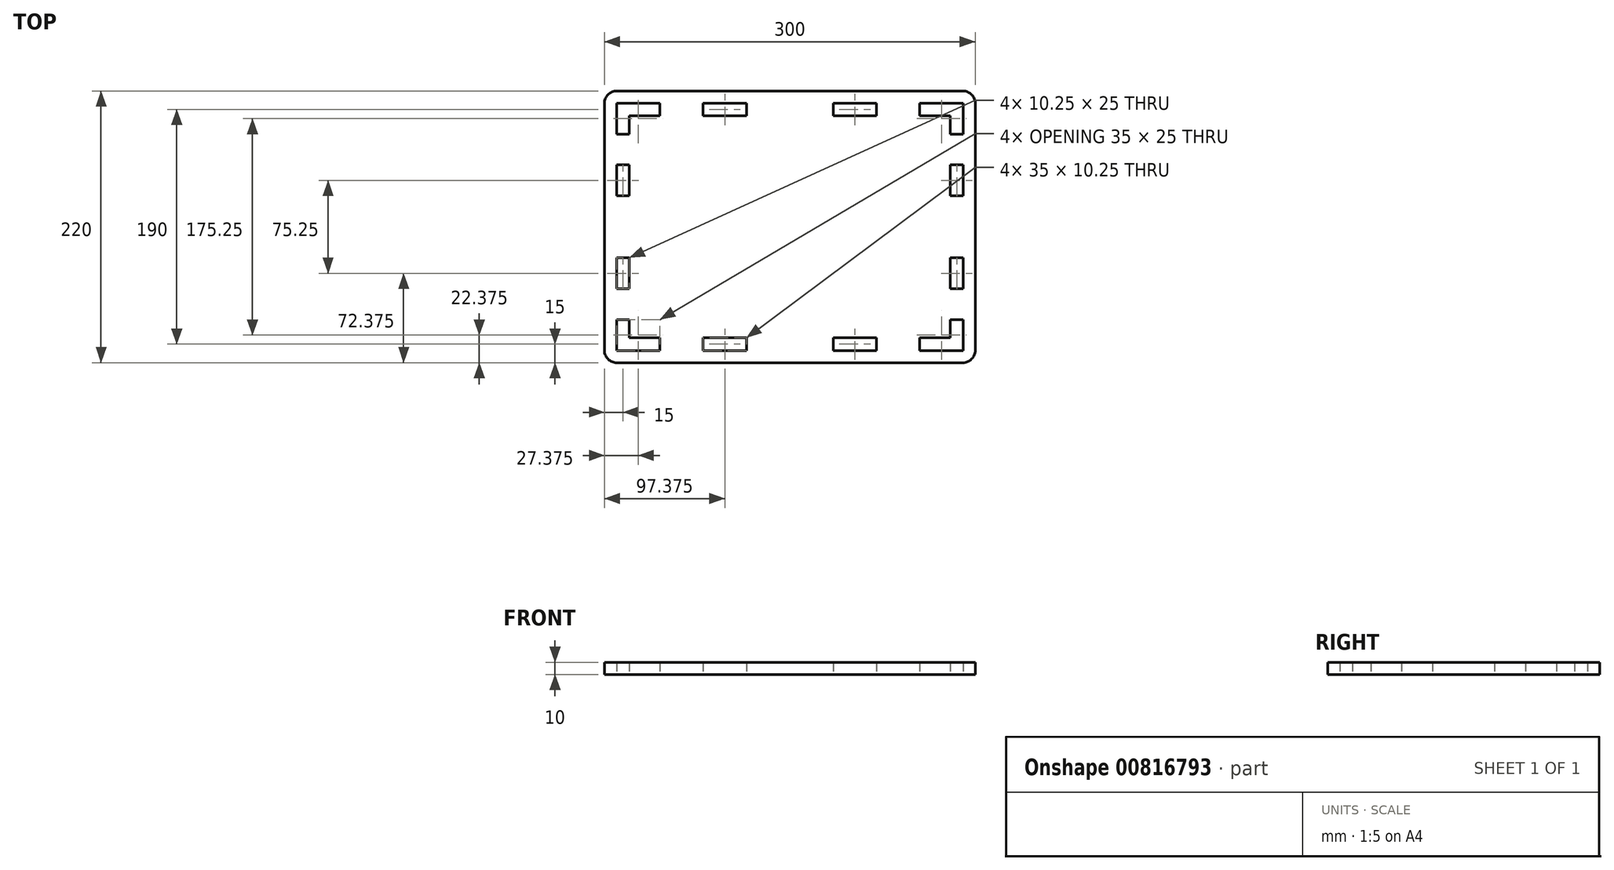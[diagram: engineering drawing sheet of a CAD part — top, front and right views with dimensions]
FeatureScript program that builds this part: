
annotation { "Feature Type Name" : "Feature", "Feature Type Description" : "" }
export const myFeature = defineFeature(function(context is Context, id is Id, definition is map)
    precondition{}
    {
        {
            var Q0;
            Q0=qCreatedBy(makeId("Top.planeOp"),FACE);
            var sketch = newSketch(context, id + "F0", { "sketchPlane" : qUnion([Q0])});
            skLineSegment(sketch, "E0.bottom", {"start": v(-140, 110) * mm, "end": v(140, 110) * mm});
            skLineSegment(sketch, "E0.top", {"start": v(-140, -110) * mm, "end": v(140, -110) * mm});
            skLineSegment(sketch, "E0.left", {"start": v(-150, 100) * mm, "end": v(-150, -100) * mm});
            skLineSegment(sketch, "E0.right", {"start": v(150, 100) * mm, "end": v(150, -100) * mm});
            skPoint(sketch, "E1.middle", {"position": v(0, 0) * mm});
            skLineSegment(sketch, "E2", {"start": v(-140.12, -100.12) * mm, "end": v(-105.13, -100.12) * mm});
            skLineSegment(sketch, "E3", {"start": v(-140.12, -100.12) * mm, "end": v(-140.12, -75.12) * mm});
            skLineSegment(sketch, "E4", {"start": v(-140.12, -75.12) * mm, "end": v(-129.88, -75.12) * mm});
            skLineSegment(sketch, "E5", {"start": v(-129.88, -75.12) * mm, "end": v(-129.88, -89.88) * mm});
            skLineSegment(sketch, "E6", {"start": v(-140.12, -50.12) * mm, "end": v(-129.88, -50.12) * mm});
            skLineSegment(sketch, "E7", {"start": v(-129.88, -50.12) * mm, "end": v(-129.88, -25.12) * mm});
            skLineSegment(sketch, "E8", {"start": v(-129.88, -25.12) * mm, "end": v(-140.12, -25.12) * mm});
            skLineSegment(sketch, "E9", {"start": v(-140.12, -25.12) * mm, "end": v(-140.12, -50.12) * mm});
            skLineSegment(sketch, "E10", {"start": v(-105.13, -100.12) * mm, "end": v(-105.13, -89.87) * mm});
            skLineSegment(sketch, "E11", {"start": v(-105.13, -89.87) * mm, "end": v(-129.88, -89.88) * mm});
            skLineSegment(sketch, "E12.MirrorCS", {"start": v(140.12, -75.12) * mm, "end": v(129.88, -75.12) * mm});
            skLineSegment(sketch, "E13.MirrorCS", {"start": v(129.88, -75.12) * mm, "end": v(129.88, -89.88) * mm});
            skLineSegment(sketch, "E14.MirrorCS", {"start": v(105.13, -89.87) * mm, "end": v(129.88, -89.88) * mm});
            skLineSegment(sketch, "E15.MirrorCS", {"start": v(105.13, -100.12) * mm, "end": v(105.13, -89.87) * mm});
            skLineSegment(sketch, "E16.MirrorCS", {"start": v(140.12, -100.12) * mm, "end": v(105.13, -100.12) * mm});
            skLineSegment(sketch, "E17.MirrorCS", {"start": v(140.12, -100.12) * mm, "end": v(140.12, -75.12) * mm});
            skLineSegment(sketch, "E18", {"start": v(-70.13, -100.12) * mm, "end": v(-70.13, -89.87) * mm});
            skLineSegment(sketch, "E19", {"start": v(-70.13, -89.87) * mm, "end": v(-35.13, -89.87) * mm});
            skLineSegment(sketch, "E20", {"start": v(-35.13, -89.87) * mm, "end": v(-35.13, -100.12) * mm});
            skLineSegment(sketch, "E21", {"start": v(-70.13, -100.12) * mm, "end": v(-35.13, -100.12) * mm});
            skLineSegment(sketch, "E22.MirrorCS", {"start": v(70.13, -89.87) * mm, "end": v(35.13, -89.87) * mm});
            skLineSegment(sketch, "E23.MirrorCS", {"start": v(70.13, -100.12) * mm, "end": v(70.13, -89.87) * mm});
            skLineSegment(sketch, "E24.MirrorCS", {"start": v(70.13, -100.12) * mm, "end": v(35.13, -100.12) * mm});
            skLineSegment(sketch, "E25.MirrorCS", {"start": v(35.13, -89.87) * mm, "end": v(35.13, -100.12) * mm});
            skLineSegment(sketch, "E26.MirrorCS", {"start": v(105.13, 100.12) * mm, "end": v(105.13, 89.87) * mm});
            skLineSegment(sketch, "E27.MirrorCS", {"start": v(-70.13, 100.12) * mm, "end": v(-70.13, 89.87) * mm});
            skLineSegment(sketch, "E28.MirrorCS", {"start": v(140.12, 75.12) * mm, "end": v(129.88, 75.12) * mm});
            skLineSegment(sketch, "E29.MirrorCS", {"start": v(70.13, 100.12) * mm, "end": v(70.13, 89.87) * mm});
            skLineSegment(sketch, "E30.MirrorCS", {"start": v(-35.13, 89.87) * mm, "end": v(-35.13, 100.12) * mm});
            skLineSegment(sketch, "E31.MirrorCS", {"start": v(-140.12, 75.12) * mm, "end": v(-129.88, 75.12) * mm});
            skLineSegment(sketch, "E32.MirrorCS", {"start": v(35.13, 89.87) * mm, "end": v(35.13, 100.12) * mm});
            skLineSegment(sketch, "E33.MirrorCS", {"start": v(-105.13, 100.12) * mm, "end": v(-105.13, 89.87) * mm});
            skLineSegment(sketch, "E34.MirrorCS", {"start": v(140.12, 100.12) * mm, "end": v(105.13, 100.12) * mm});
            skLineSegment(sketch, "E35.MirrorCS", {"start": v(-140.12, 100.12) * mm, "end": v(-140.12, 75.12) * mm});
            skLineSegment(sketch, "E36.MirrorCS", {"start": v(-70.13, 100.12) * mm, "end": v(-35.13, 100.12) * mm});
            skLineSegment(sketch, "E37.MirrorCS", {"start": v(-105.13, 89.87) * mm, "end": v(-129.88, 89.88) * mm});
            skLineSegment(sketch, "E38.MirrorCS", {"start": v(-140.12, 100.12) * mm, "end": v(-105.13, 100.12) * mm});
            skLineSegment(sketch, "E39.MirrorCS", {"start": v(-70.13, 89.87) * mm, "end": v(-35.13, 89.87) * mm});
            skLineSegment(sketch, "E40.MirrorCS", {"start": v(129.88, 75.12) * mm, "end": v(129.88, 89.88) * mm});
            skLineSegment(sketch, "E41.MirrorCS", {"start": v(70.13, 100.12) * mm, "end": v(35.13, 100.12) * mm});
            skLineSegment(sketch, "E42.MirrorCS", {"start": v(70.13, 89.87) * mm, "end": v(35.13, 89.87) * mm});
            skLineSegment(sketch, "E43.MirrorCS", {"start": v(105.13, 89.87) * mm, "end": v(129.88, 89.88) * mm});
            skLineSegment(sketch, "E44.MirrorCS", {"start": v(-129.88, 75.12) * mm, "end": v(-129.88, 89.88) * mm});
            skLineSegment(sketch, "E45.MirrorCS", {"start": v(140.12, 100.12) * mm, "end": v(140.12, 75.12) * mm});
            skLineSegment(sketch, "E46.MirrorCS", {"start": v(-129.88, 25.12) * mm, "end": v(-140.12, 25.12) * mm});
            skLineSegment(sketch, "E47.MirrorCS", {"start": v(-140.12, 25.12) * mm, "end": v(-140.12, 50.12) * mm});
            skLineSegment(sketch, "E48.MirrorCS", {"start": v(-140.12, 50.12) * mm, "end": v(-129.88, 50.12) * mm});
            skLineSegment(sketch, "E49.MirrorCS", {"start": v(-129.88, 50.12) * mm, "end": v(-129.88, 25.12) * mm});
            skLineSegment(sketch, "E50.MirrorCS", {"start": v(140.12, 50.12) * mm, "end": v(129.88, 50.12) * mm});
            skLineSegment(sketch, "E51.MirrorCS", {"start": v(140.12, 25.12) * mm, "end": v(140.12, 50.12) * mm});
            skLineSegment(sketch, "E52.MirrorCS", {"start": v(129.88, 50.12) * mm, "end": v(129.88, 25.12) * mm});
            skLineSegment(sketch, "E53.MirrorCS", {"start": v(129.88, 25.12) * mm, "end": v(140.12, 25.12) * mm});
            skLineSegment(sketch, "E54.MirrorCS", {"start": v(129.88, -25.12) * mm, "end": v(140.12, -25.12) * mm});
            skLineSegment(sketch, "E55.MirrorCS", {"start": v(140.12, -25.12) * mm, "end": v(140.12, -50.12) * mm});
            skLineSegment(sketch, "E56.MirrorCS", {"start": v(140.12, -50.12) * mm, "end": v(129.88, -50.12) * mm});
            skLineSegment(sketch, "E57.MirrorCS", {"start": v(129.88, -50.12) * mm, "end": v(129.88, -25.12) * mm});
            skPoint(sketch, "E58.visualSharp", {"position": v(-150, 110) * mm});
            skArc(sketch, "E58.filletArc", {"start": v(-140, 110) * mm, "mid": v(-147.07, 107.07) * mm, "end": v(-150, 100) * mm});
            skPoint(sketch, "E59.visualSharp", {"position": v(-150, -110) * mm});
            skArc(sketch, "E59.filletArc", {"start": v(-150, -100) * mm, "mid": v(-147.07, -107.07) * mm, "end": v(-140, -110) * mm});
            skPoint(sketch, "E60.visualSharp", {"position": v(150, 110) * mm});
            skArc(sketch, "E60.filletArc", {"start": v(150, 100) * mm, "mid": v(147.07, 107.07) * mm, "end": v(140, 110) * mm});
            skPoint(sketch, "E61.visualSharp", {"position": v(150, -110) * mm});
            skArc(sketch, "E61.filletArc", {"start": v(140, -110) * mm, "mid": v(147.07, -107.07) * mm, "end": v(150, -100) * mm});
            skSolve(sketch);
        }
        {
            var Q0;
            Q0=makeQuery(id+"F0.imprint","IMPRINT",FACE,{"disambiguationData":[TD([[makeQuery(id+"F0.imprint","IMPRINT",EDGE,{"derivedFrom":sQuery(id+"F0.wireOp",EDGE,"E0.bottom")}),-1.0]])]});
            extrude(context, id + "F1", {"entities" : qUnion([Q0]), "depth" : 10 * mm, "offsetDistance" : 25 * mm});
        }
    });
